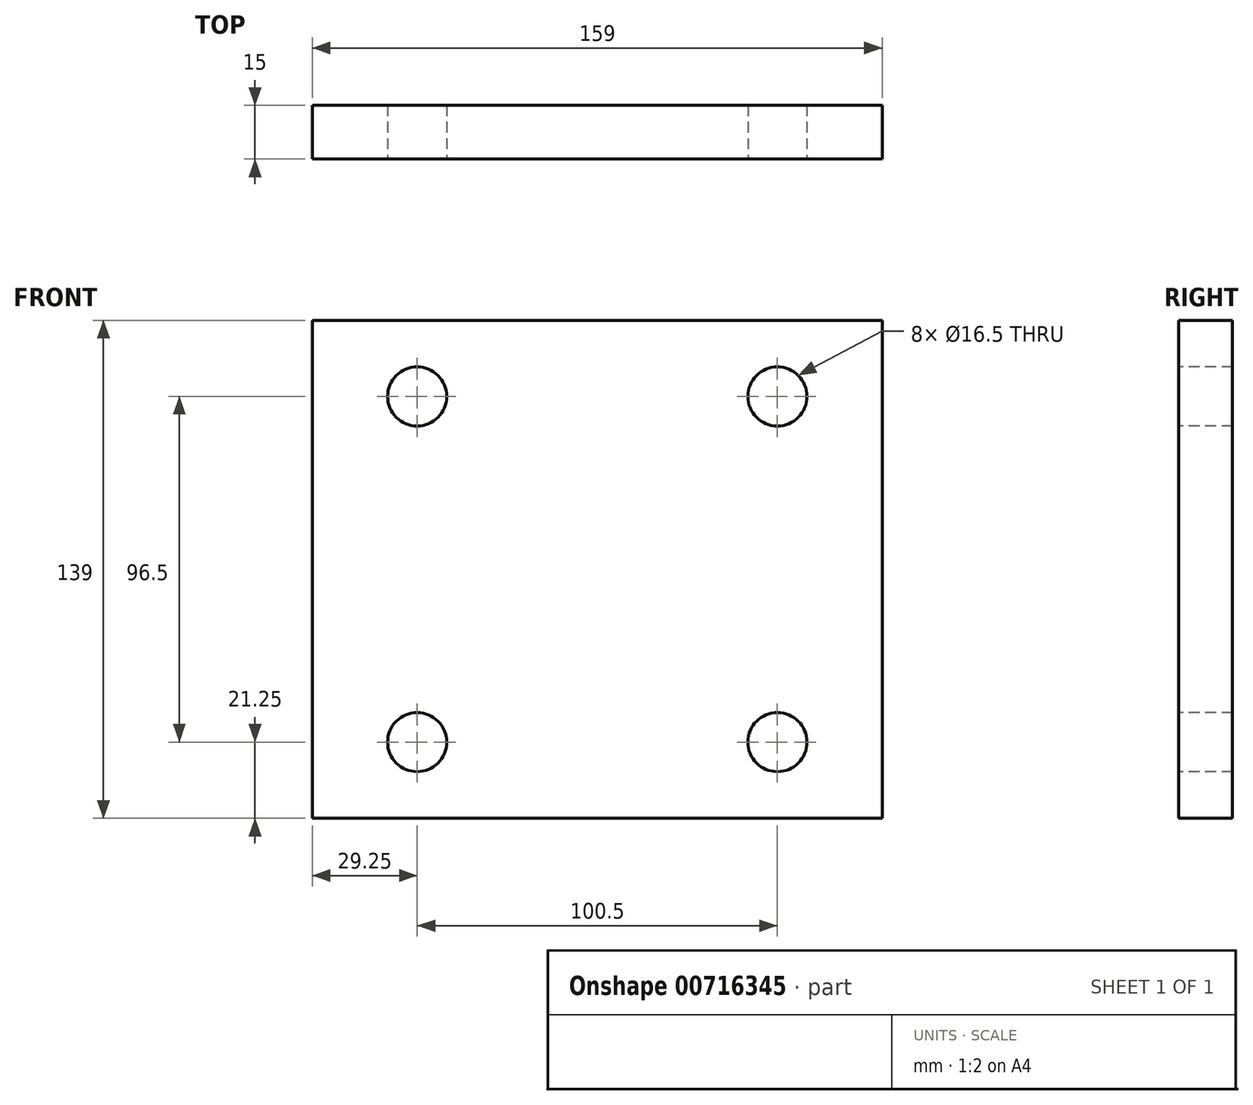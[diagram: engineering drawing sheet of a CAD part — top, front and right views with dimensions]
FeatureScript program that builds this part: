
annotation { "Feature Type Name" : "Feature", "Feature Type Description" : "" }
export const myFeature = defineFeature(function(context is Context, id is Id, definition is map)
    precondition{}
    {
        {
            var Q0;
            Q0=qCreatedBy(makeId("Front.planeOp"),FACE);
            var sketch = newSketch(context, id + "F0", { "sketchPlane" : qUnion([Q0])});
            skLineSegment(sketch, "E0.bottom", {"start": v(-79.5, 69.5) * mm, "end": v(79.5, 69.5) * mm});
            skLineSegment(sketch, "E0.top", {"start": v(-79.5, -69.5) * mm, "end": v(79.5, -69.5) * mm});
            skLineSegment(sketch, "E0.left", {"start": v(-79.5, 69.5) * mm, "end": v(-79.5, -69.5) * mm});
            skLineSegment(sketch, "E0.right", {"start": v(79.5, 69.5) * mm, "end": v(79.5, -69.5) * mm});
            skSolve(sketch);
        }
        {
            var Q0;
            Q0 = qSketchRegion(id + "F0", true);
            extrude(context, id + "F1", {"entities" : qUnion([Q0]), "depth" : 15 * mm, "offsetDistance" : 25 * mm});
        }
        {
            var Q0;
            Q0=makeQuery(id+"F1.opExtrude","CAP_FACE",FACE,{"disambiguationData":[OSD([sQuery(id+"F0.wireOp",EDGE,"E0.bottom"),sQuery(id+"F0.wireOp",EDGE,"E0.top"),sQuery(id+"F0.wireOp",EDGE,"E0.left"),sQuery(id+"F0.wireOp",EDGE,"E0.right")])],"isStart":false});
            var sketch = newSketch(context, id + "F2", { "sketchPlane" : qUnion([Q0])});
            skPoint(sketch, "E1", {"position": v(-50.25, 48.25) * mm});
            skPoint(sketch, "E2", {"position": v(50.25, 48.25) * mm});
            skPoint(sketch, "E3.MirrorP", {"position": v(-50.25, -48.25) * mm});
            skPoint(sketch, "E4.MirrorP", {"position": v(50.25, -48.25) * mm});
            skSolve(sketch);
        }
        {
            var Q0;
            Q0=sQuery(id+"F2.wireOp",VERTEX,"E1");
            var Q1;
            Q1=sQuery(id+"F2.wireOp",VERTEX,"E2");
            var Q2;
            Q2=sQuery(id+"F2.wireOp",VERTEX,"E4.MirrorP");
            var Q3;
            Q3=sQuery(id+"F2.wireOp",VERTEX,"E3.MirrorP");
            var Q4;
            Q4=makeQuery(id+"F1.opExtrude","SWEPT_BODY",BODY,{"disambiguationData":[OSD([sQuery(id+"F0.wireOp",EDGE,"E0.bottom"),sQuery(id+"F0.wireOp",EDGE,"E0.top"),sQuery(id+"F0.wireOp",EDGE,"E0.left"),sQuery(id+"F0.wireOp",EDGE,"E0.right")])]});
            hole(context, id + "F3", {"style" : HoleStyle.SIMPLE, "endStyle" : HoleEndStyle.THROUGH, "holeDiameter" : 16.5 * mm, "majorDiameter" : 5 * mm, "isTappedThrough" : true, "tappedDepth" : 12 * mm, "tapClearance" : 3, "locations" : qUnion([Q0, Q1, Q2, Q3]), "scope" : qUnion([Q4])});
        }
    });
